# Revit family: WSW260
name_source: partatom
category: Plumbing Fixtures
units: mm (PartAtom-declared; Revit-internal decimal feet)

## family parameters
Cut with Voids When Loaded = No
Host = Face
Maintain Annotation Orientation = No
OmniClass Number = 23.45.05.14.14
OmniClass Title = Sinks/Lavatories
Part Type = Normal
Room Calculation Point = No
Round Connector Dimension = Use Diameter
Shared = Yes

## types (2) — shared parameters
ADA Compliant = Yes
Assembly Code = D2010440
Body Material = Metal-Acorn-304-Stainless_Steel-16-Gauge
Bowl Shape = Trough
CW Connection = Yes
CWFU = 3
Cold Water Connection Diameter = 1 5/16"
Cold Water Connection Radius = 21/32"
Default Elevation = 34"
Description = Neo-Metro® by Acorn® provides this durable, stainless steel trough sink. It is available in sizes to accommodate from one to four users. The design is perfect for high-traffic restrooms, incorporating ample personal space while reducing wet, slippery floors.

The WSW000 Series hand washing station is wall mounted and features a unique “wedge”-shaped trough (patent pending) with a polished stainless steel finish and rounded corners.

Optional trap enclosures are available to conceal hot and cold mixing valves and supply/waste connections while providing easy maintenance access. The enclosure is fabricated of 16 gauge, type 304 stainless steel with a satin finish. It is available in 24" (610 mm) or 54" (1,372 mm) widths.

When mounted at 34" (864 mm) from the finished floor, the fixture will comply with ANSI, UFAS, CBC, OBC, and ADA requirements. Compliance is subject to the interpretation and requirements of the local code authority.
Diameter For Soap Knockout = 1 3/8"
EG - Enviro-Glaze, Specify Color = No
Flow Rate = 0.5 GPM (1.9 LPM) for faucet type
HW Connection = Yes
HWFU = 3
Height = 19 1/4"
Hot Water Connection Diameter = 1 5/16"
Hot Water Connection Radius = 21/32"
IAPMO Compliance = ixture complies with ANSI, UFAS, CBC and ADA 2010 requirements for accessibility
Installation Type = Wall Mounted
Length = 60"
Manufacturer = Acorn Engineering
Model = WSW260
PS1000 - PS Pump Soap Dispenser, Specify number = No
Price = Prices may vary. Please consult Manufacturer Representative for most up-to-date price list.
Product Documentation Link = https://www.acorneng.com
Product Page URL = https://www.acorneng.com
SW000 - F50 H&C Wristblade Faucet, Gooseneck Spout = No
SW000 - F51 H&C Wristblade Faucet, Spout = No
SW000 - F60 S/T Sensor Operated Faucet,J Spout, Plate = No
SW000 - F70 S/T Pushbutton Metering Faucet, Plate = No
SW000 - PT Daisy Strainer, Tailpiece, 1-1/2” P-Trap, Plastic = No
SW000 - PTC Daisy Strainer, Tailpiece, 1-1/2” P-Trap, Chrome = No
Sink Inner Length = 57 7/8"
Sink Inner Width = 15 3/4"
Type Comments = WEDGE™ Stainless Steel Trough Sink
URL = https://acorneng.com
Vent Connection = No
WFU = 4
Waste Connection = Yes
Waste Connection Diameter = 1 1/2"
Waste Connection Radius = 3/4"
Width = 21 5/8"

## per-type parameters (varying)
| type | DSW000-TC1Accessory: Single 24" Wide Trap Enclosure | DSW000-TC2Accessory: Single 54" Wide Trap Enclosure | Trap Enclosure Width |
| WSW260-TC1 | Yes | No | 24" |
| WSW260-TC2 | No | Yes | 54" |

## geometry (parser evidence)
native form markers: Sweep x2
no freeform markers — native parametric forms only
